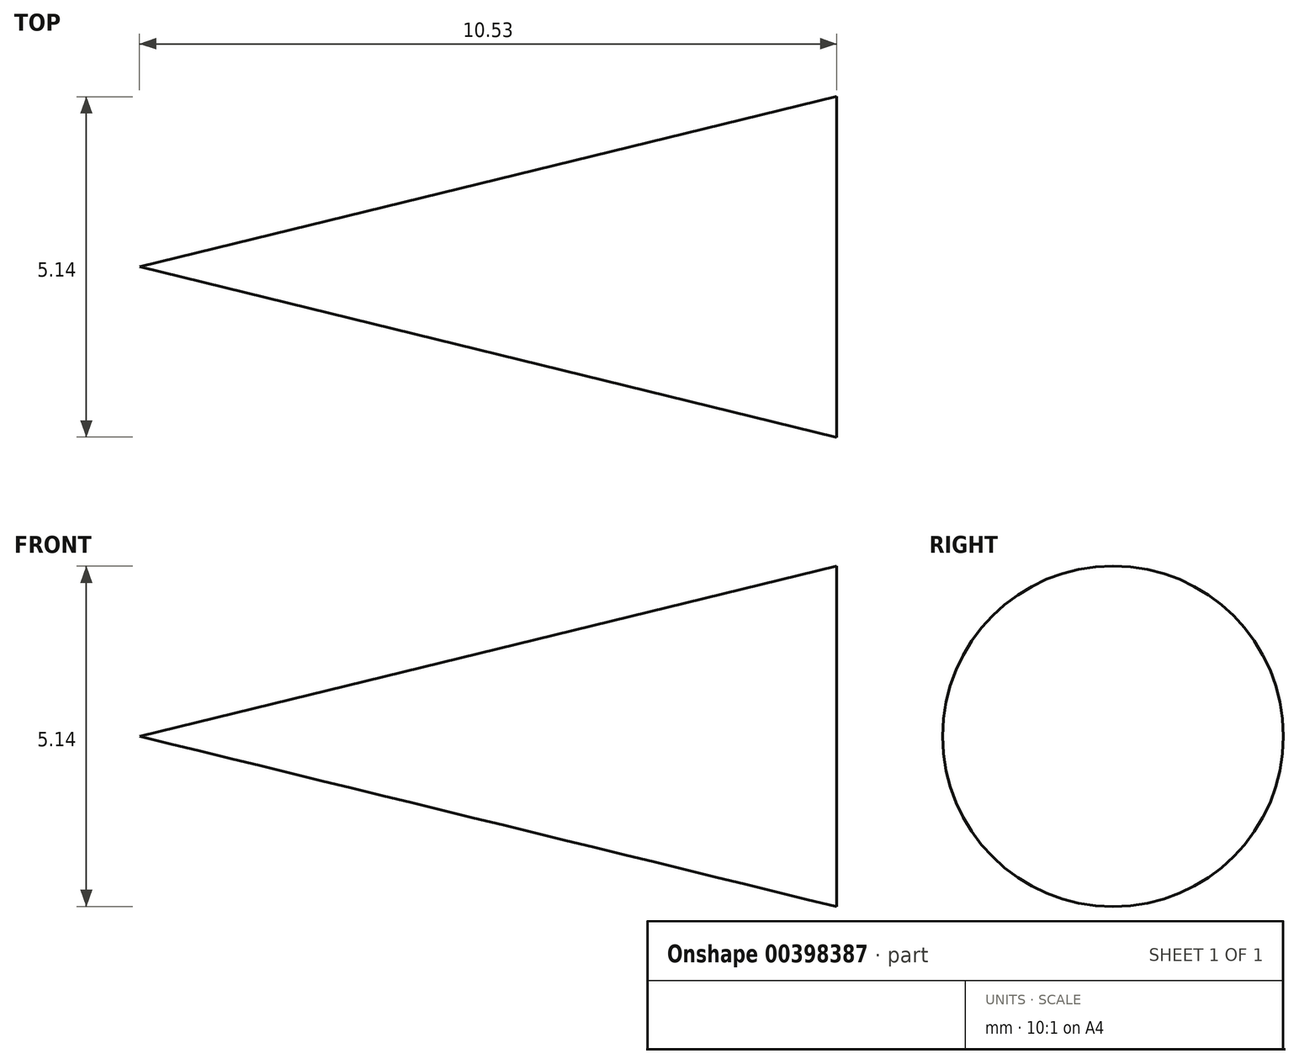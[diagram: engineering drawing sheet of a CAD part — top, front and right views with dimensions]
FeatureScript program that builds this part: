
annotation { "Feature Type Name" : "Feature", "Feature Type Description" : "" }
export const myFeature = defineFeature(function(context is Context, id is Id, definition is map)
    precondition{}
    {
        {
            var Q0;
            Q0=qCreatedBy(makeId("Front.planeOp"),FACE);
            var sketch = newSketch(context, id + "F0", { "sketchPlane" : qUnion([Q0])});
            skLineSegment(sketch, "E0", {"start": v(0, 0) * mm, "end": v(-10.53, 0) * mm});
            skLineSegment(sketch, "E1", {"start": v(-10.53, 0) * mm, "end": v(0, 2.57) * mm});
            skLineSegment(sketch, "E2", {"start": v(0, 2.57) * mm, "end": v(0, 0) * mm});
            skSolve(sketch);
        }
        {
            var Q0;
            Q0 = qSketchRegion(id + "F0", true);
            var Q1;
            Q1=sQuery(id+"F0.wireOp",EDGE,"E0");
            revolve(context, id + "F1", {"entities" : qUnion([Q0]), "axis" : qUnion([Q1]), "revolveType" : RevolveType.FULL});
        }
    });
